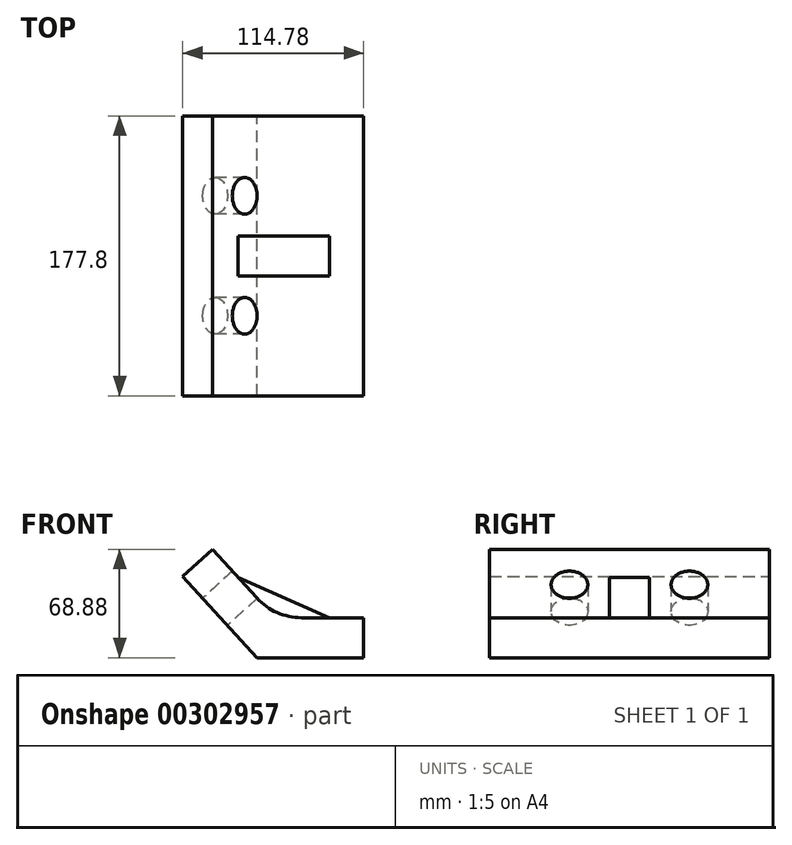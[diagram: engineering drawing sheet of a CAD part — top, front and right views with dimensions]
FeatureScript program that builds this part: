
annotation { "Feature Type Name" : "Feature", "Feature Type Description" : "" }
export const myFeature = defineFeature(function(context is Context, id is Id, definition is map)
    precondition{}
    {
        {
            var Q0;
            Q0=qCreatedBy(makeId("Front.planeOp"),FACE);
            var sketch = newSketch(context, id + "F0", { "sketchPlane" : qUnion([Q0])});
            skLineSegment(sketch, "E0", {"start": v(0, 0) * mm, "end": v(67.55, 0) * mm});
            skLineSegment(sketch, "E1", {"start": v(67.55, 0) * mm, "end": v(67.55, 25.4) * mm});
            skLineSegment(sketch, "E2", {"start": v(67.55, 25.4) * mm, "end": v(28.02, 25.4) * mm});
            skLineSegment(sketch, "E3", {"start": v(-0.12, 37.82) * mm, "end": v(-28.47, 68.88) * mm});
            skLineSegment(sketch, "E4", {"start": v(-28.47, 68.88) * mm, "end": v(-47.23, 51.76) * mm});
            skLineSegment(sketch, "E5", {"start": v(-47.23, 51.76) * mm, "end": v(0, 0) * mm});
            skPoint(sketch, "E6.visualSharp", {"position": v(11.2, 25.4) * mm});
            skArc(sketch, "E6.filletArc", {"start": v(-0.12, 37.82) * mm, "mid": v(12.64, 28.64) * mm, "end": v(28.02, 25.4) * mm});
            skSolve(sketch);
        }
        {
            var Q0;
            Q0 = qSketchRegion(id + "F0", true);
            extrude(context, id + "F1", {"entities" : qUnion([Q0]), "endBound" : BoundingType.SYMMETRIC, "depth" : 177.8 * mm});
        }
        {
            var Q0;
            Q0=qCreatedBy(makeId("Front.planeOp"),FACE);
            var sketch = newSketch(context, id + "F2", { "sketchPlane" : qUnion([Q0])});
            skLineSegment(sketch, "E7", {"start": v(-35.58, 76.67) * mm, "end": v(11.2, 25.4) * mm});
            skLineSegment(sketch, "E8", {"start": v(11.2, 25.4) * mm, "end": v(66.7, 25.4) * mm});
            skLineSegment(sketch, "E9", {"start": v(11.2, 25.4) * mm, "end": v(-12.18, 51.04) * mm});
            skPoint(sketch, "E9.endSnap0", {"position": v(-12.18, 51.04) * mm});
            skLineSegment(sketch, "E10", {"start": v(-12.18, 51.04) * mm, "end": v(45.91, 25.4) * mm});
            skLineSegment(sketch, "E11", {"start": v(45.91, 25.4) * mm, "end": v(11.2, 25.4) * mm});
            skSolve(sketch);
        }
        {
            var Q0;
            Q0 = qSketchRegion(id + "F2", true);
            extrude(context, id + "F3", {"entities" : qUnion([Q0]), "operationType" : NewBodyOperationType.ADD, "endBound" : BoundingType.SYMMETRIC, "depth" : 25.4 * mm});
        }
        {
            var Q0;
            Q0=makeQuery(id+"F1.opExtrude","SWEPT_FACE",FACE,{"disambiguationData":[OSD([sQuery(id+"F0.wireOp",EDGE,"E5")])]});
            var sketch = newSketch(context, id + "F4", { "sketchPlane" : qUnion([Q0])});
            skCircle(sketch, "E12", {"center": v(-38.1, 39.6) * mm, "radius": 11.67 * mm});
            skCircle(sketch, "E13", {"center": v(38.1, 39.6) * mm, "radius": 11.67 * mm});
            skSolve(sketch);
        }
        {
            var Q0;
            Q0 = qSketchRegion(id + "F4", true);
            extrude(context, id + "F5", {"entities" : qUnion([Q0]), "operationType" : NewBodyOperationType.REMOVE, "endBound" : BoundingType.THROUGH_ALL, "oppositeDirection" : true, "depth" : 25.4 * mm});
        }
    });
